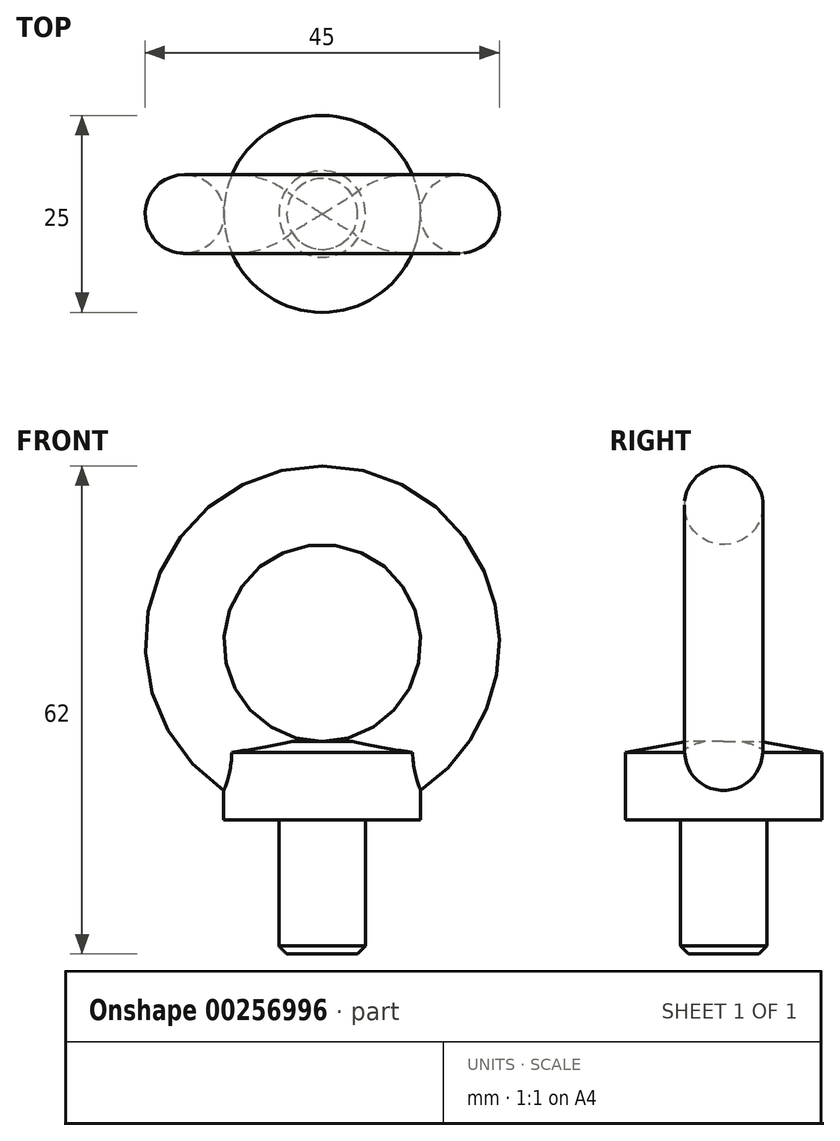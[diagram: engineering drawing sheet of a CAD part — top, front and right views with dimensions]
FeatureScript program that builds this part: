
annotation { "Feature Type Name" : "Feature", "Feature Type Description" : "" }
export const myFeature = defineFeature(function(context is Context, id is Id, definition is map)
    precondition{}
    {
        {
            var Q0;
            Q0=qCreatedBy(makeId("Top.planeOp"),FACE);
            cPlane(context, id + "F0", {"entities" : qUnion([Q0]), "cplaneType" : CPlaneType.OFFSET, "offset" : 22.5 * mm, "oppositeDirection" : true, "width" : 150 * mm, "height" : 150 * mm});
        }
        {
            var Q0;
            Q0=qCreatedBy(id+"F0.planeOp",FACE);
            var sketch = newSketch(context, id + "F1", { "sketchPlane" : qUnion([Q0])});
            skCircle(sketch, "E0", {"center": v(0, 0) * mm, "radius": 12.5 * mm});
            skSolve(sketch);
        }
        {
            var Q0;
            Q0=qCreatedBy(makeId("Top.planeOp"),FACE);
            var sketch = newSketch(context, id + "F2", { "sketchPlane" : qUnion([Q0])});
            skCircle(sketch, "E1", {"center": v(17.5, 0) * mm, "radius": 5 * mm});
            skLineSegment(sketch, "E2", {"start": v(0, 18.88) * mm, "end": v(0, -13.7) * mm, "construction": true});
            skSolve(sketch);
        }
        {
            var Q0;
            Q0 = qSketchRegion(id + "F1", true);
            extrude(context, id + "F3", {"entities" : qUnion([Q0]), "depth" : 10 * mm});
        }
        {
            var Q0;
            Q0=makeQuery(id+"F3.opExtrude","CAP_EDGE",EDGE,{"disambiguationData":[OSD([sQuery(id+"F1.wireOp",EDGE,"E0")])],"isStart":false});
            chamfer(context, id + "F4", {"entities" : qUnion([Q0]), "chamferType" : ChamferType.OFFSET_ANGLE, "width" : 8 * mm, "oppositeDirection" : false, "angle" : 10 * degree, "tangentPropagation" : true});
        }
        {
            var Q0;
            Q0 = qSketchRegion(id + "F2", true);
            var Q1;
            Q1=sQuery(id+"F2.wireOp",EDGE,"E2");
            revolve(context, id + "F5", {"operationType" : NewBodyOperationType.ADD, "entities" : qUnion([Q0]), "axis" : qUnion([Q1]), "revolveType" : RevolveType.FULL});
        }
        {
            var Q0;
            Q0=makeQuery(id+"F3.opExtrude","CAP_FACE",FACE,{"disambiguationData":[OSD([sQuery(id+"F1.wireOp",EDGE,"E0")])],"isStart":true});
            var sketch = newSketch(context, id + "F6", { "sketchPlane" : qUnion([Q0])});
            skCircle(sketch, "E3", {"center": v(0, 0) * mm, "radius": 5.5 * mm});
            skSolve(sketch);
        }
        {
            var Q0;
            Q0 = qSketchRegion(id + "F6", true);
            extrude(context, id + "F7", {"entities" : qUnion([Q0]), "operationType" : NewBodyOperationType.ADD, "depth" : 17 * mm});
        }
        {
            var Q0;
            Q0=makeQuery(id+"F7.opExtrude","CAP_EDGE",EDGE,{"disambiguationData":[OSD([sQuery(id+"F6.wireOp",EDGE,"E3")])],"isStart":false});
            chamfer(context, id + "F8", {"entities" : qUnion([Q0]), "width" : 1 * mm, "tangentPropagation" : true});
        }
    });
